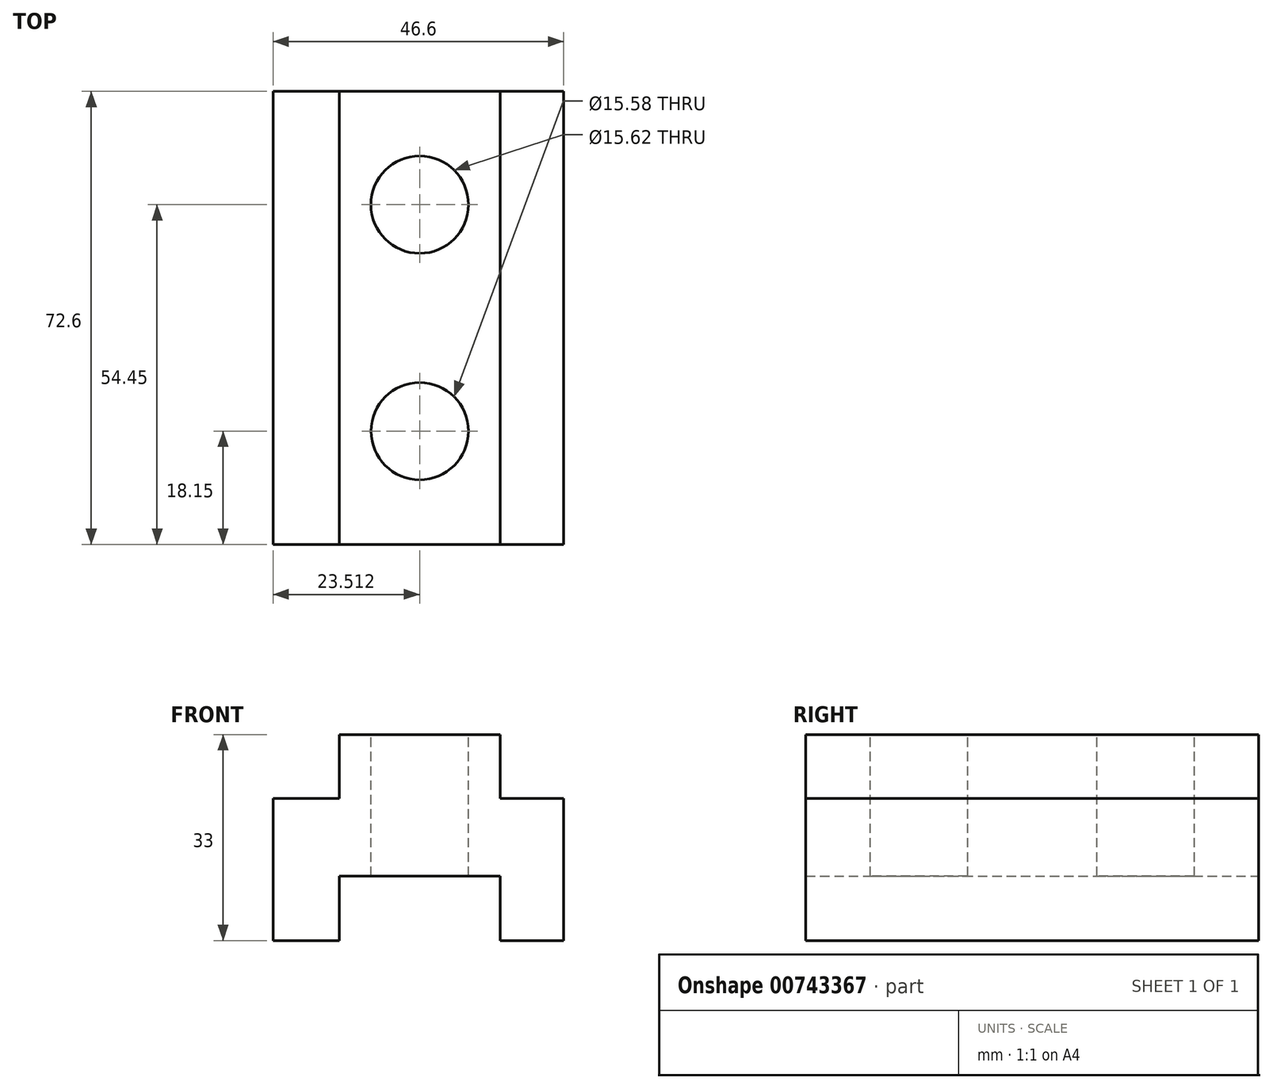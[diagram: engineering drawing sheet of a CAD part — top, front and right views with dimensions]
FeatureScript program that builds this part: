
annotation { "Feature Type Name" : "Feature", "Feature Type Description" : "" }
export const myFeature = defineFeature(function(context is Context, id is Id, definition is map)
    precondition{}
    {
        {
            var Q0;
            Q0=qCreatedBy(makeId("Front.planeOp"),FACE);
            var sketch = newSketch(context, id + "F0", { "sketchPlane" : qUnion([Q0])});
            skLineSegment(sketch, "E0", {"start": v(0, 0) * mm, "end": v(10.62, 0) * mm});
            skLineSegment(sketch, "E1", {"start": v(10.62, 0) * mm, "end": v(10.62, 10.34) * mm});
            skLineSegment(sketch, "E2", {"start": v(10.62, 10.34) * mm, "end": v(36.4, 10.34) * mm});
            skLineSegment(sketch, "E3", {"start": v(36.4, 10.34) * mm, "end": v(36.4, 0) * mm});
            skLineSegment(sketch, "E4", {"start": v(36.4, 0) * mm, "end": v(46.6, 0) * mm});
            skLineSegment(sketch, "E5", {"start": v(46.6, 0) * mm, "end": v(46.6, 22.8) * mm});
            skLineSegment(sketch, "E6", {"start": v(46.6, 22.8) * mm, "end": v(36.4, 22.8) * mm});
            skLineSegment(sketch, "E7", {"start": v(0, 0) * mm, "end": v(0, 22.8) * mm});
            skLineSegment(sketch, "E8", {"start": v(0, 22.8) * mm, "end": v(10.62, 22.8) * mm});
            skLineSegment(sketch, "E9", {"start": v(10.62, 22.8) * mm, "end": v(10.62, 33) * mm});
            skLineSegment(sketch, "E10", {"start": v(10.62, 33) * mm, "end": v(36.4, 33) * mm});
            skLineSegment(sketch, "E11", {"start": v(36.4, 33) * mm, "end": v(36.4, 22.8) * mm});
            skSolve(sketch);
        }
        {
            var Q0;
            Q0 = qSketchRegion(id + "F0", true);
            extrude(context, id + "F1", {"entities" : qUnion([Q0]), "depth" : 72.6 * mm, "offsetDistance" : 25 * mm});
        }
        {
            var Q0;
            Q0=makeQuery(id+"F1.opExtrude","SWEPT_FACE",FACE,{"disambiguationData":[OSD([sQuery(id+"F0.wireOp",EDGE,"E10")])]});
            var sketch = newSketch(context, id + "F2", { "sketchPlane" : qUnion([Q0])});
            skPoint(sketch, "E12.endSnap0", {"position": v(23.51, -72.6) * mm});
            skCircle(sketch, "E13", {"center": v(23.51, -18.15) * mm, "radius": 7.81 * mm});
            skCircle(sketch, "E14", {"center": v(23.51, -54.45) * mm, "radius": 7.8 * mm});
            skSolve(sketch);
        }
        {
            var Q0;
            Q0 = qSketchRegion(id + "F2", true);
            extrude(context, id + "F3", {"entities" : qUnion([Q0]), "operationType" : NewBodyOperationType.REMOVE, "oppositeDirection" : true, "depth" : 25 * mm, "offsetDistance" : 25 * mm});
        }
    });
